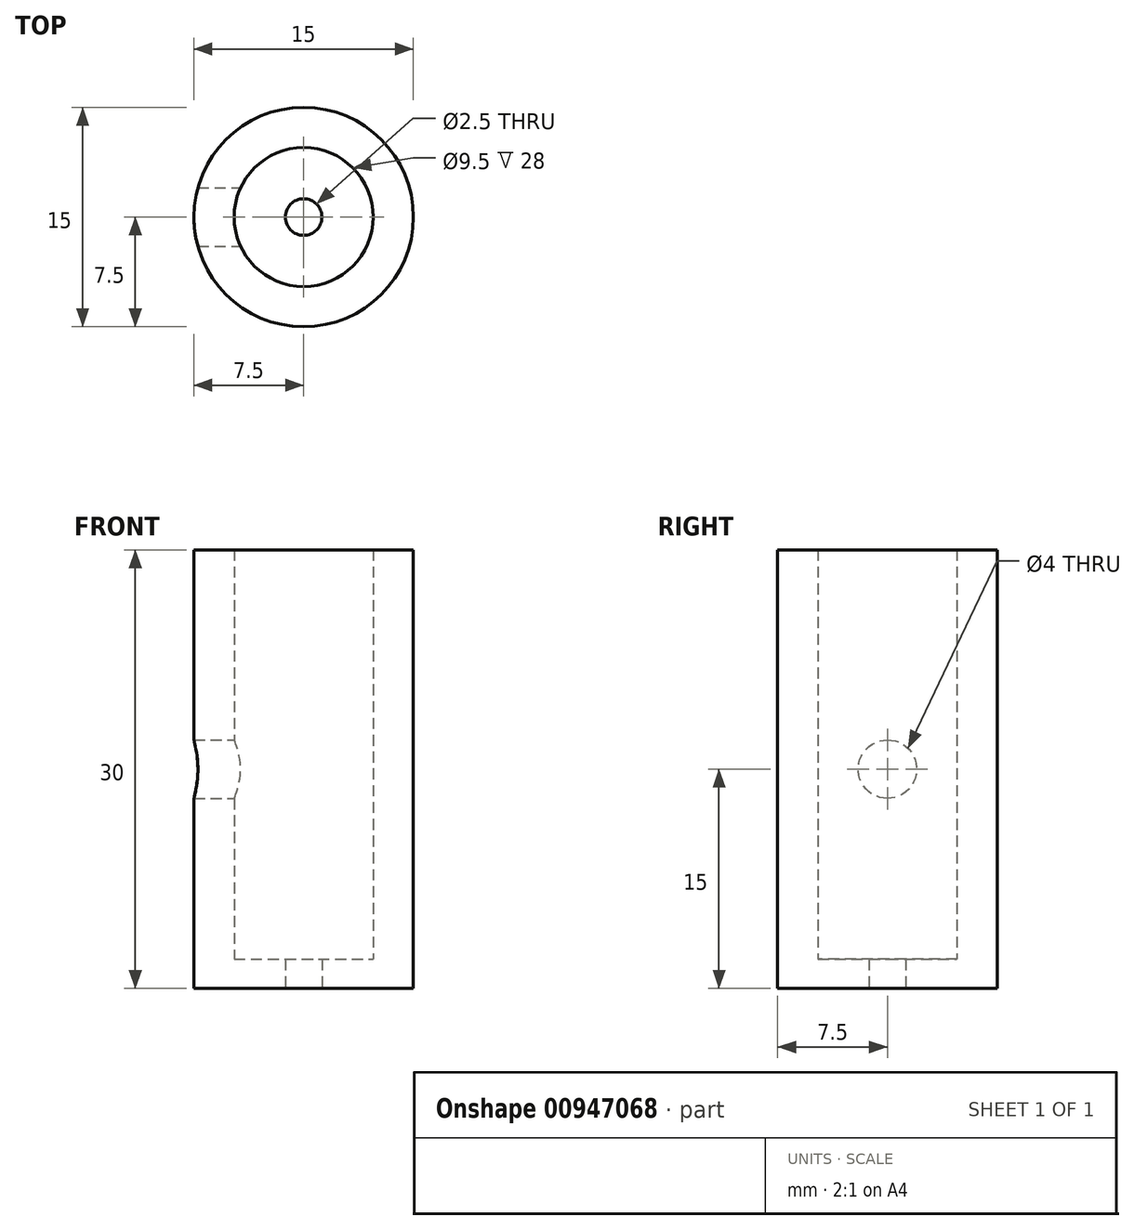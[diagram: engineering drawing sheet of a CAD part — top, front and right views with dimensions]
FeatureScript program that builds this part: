
annotation { "Feature Type Name" : "Feature", "Feature Type Description" : "" }
export const myFeature = defineFeature(function(context is Context, id is Id, definition is map)
    precondition{}
    {
        {
            var Q0;
            Q0=qCreatedBy(makeId("Right.planeOp"),FACE);
            var sketch = newSketch(context, id + "F0", { "sketchPlane" : qUnion([Q0])});
            skLineSegment(sketch, "E0", {"start": v(-1.25, 0) * mm, "end": v(-1.25, 2) * mm});
            skLineSegment(sketch, "E1", {"start": v(-1.25, 2) * mm, "end": v(-4.75, 2) * mm});
            skLineSegment(sketch, "E2", {"start": v(-4.75, 2) * mm, "end": v(-4.75, 30) * mm});
            skLineSegment(sketch, "E3", {"start": v(-4.75, 30) * mm, "end": v(-7.5, 30) * mm});
            skLineSegment(sketch, "E4", {"start": v(-7.5, 30) * mm, "end": v(-7.5, 0) * mm});
            skLineSegment(sketch, "E5", {"start": v(-7.5, 0) * mm, "end": v(-1.25, 0) * mm});
            skLineSegment(sketch, "E6", {"start": v(0, 0) * mm, "end": v(0, 7) * mm, "construction": true});
            skSolve(sketch);
        }
        {
            var Q0;
            Q0=makeQuery(id+"F0.imprint","IMPRINT",FACE,{"disambiguationData":[TD([[makeQuery(id+"F0.imprint","IMPRINT",EDGE,{"derivedFrom":sQuery(id+"F0.wireOp",EDGE,"E0")}),1.0]])]});
            var Q1;
            Q1=sQuery(id+"F0.wireOp",EDGE,"E6");
            revolve(context, id + "F1", {"surfaceOperationType" : NewSurfaceOperationType.NEW, "entities" : qUnion([Q0]), "axis" : qUnion([Q1]), "revolveType" : RevolveType.FULL});
        }
        {
            var Q0;
            Q0=qCreatedBy(makeId("Right.planeOp"),FACE);
            var sketch = newSketch(context, id + "F2", { "sketchPlane" : qUnion([Q0])});
            skLineSegment(sketch, "E7", {"start": v(0, 0) * mm, "end": v(0, 15) * mm, "construction": true});
            skCircle(sketch, "E8", {"center": v(0, 15) * mm, "radius": 2 * mm});
            skSolve(sketch);
        }
        {
            var Q0;
            Q0 = qSketchRegion(id + "F2", true);
            extrude(context, id + "F3", {"entities" : qUnion([Q0]), "operationType" : NewBodyOperationType.REMOVE, "oppositeDirection" : true, "depth" : 25 * mm, "offsetDistance" : 25 * mm});
        }
    });
